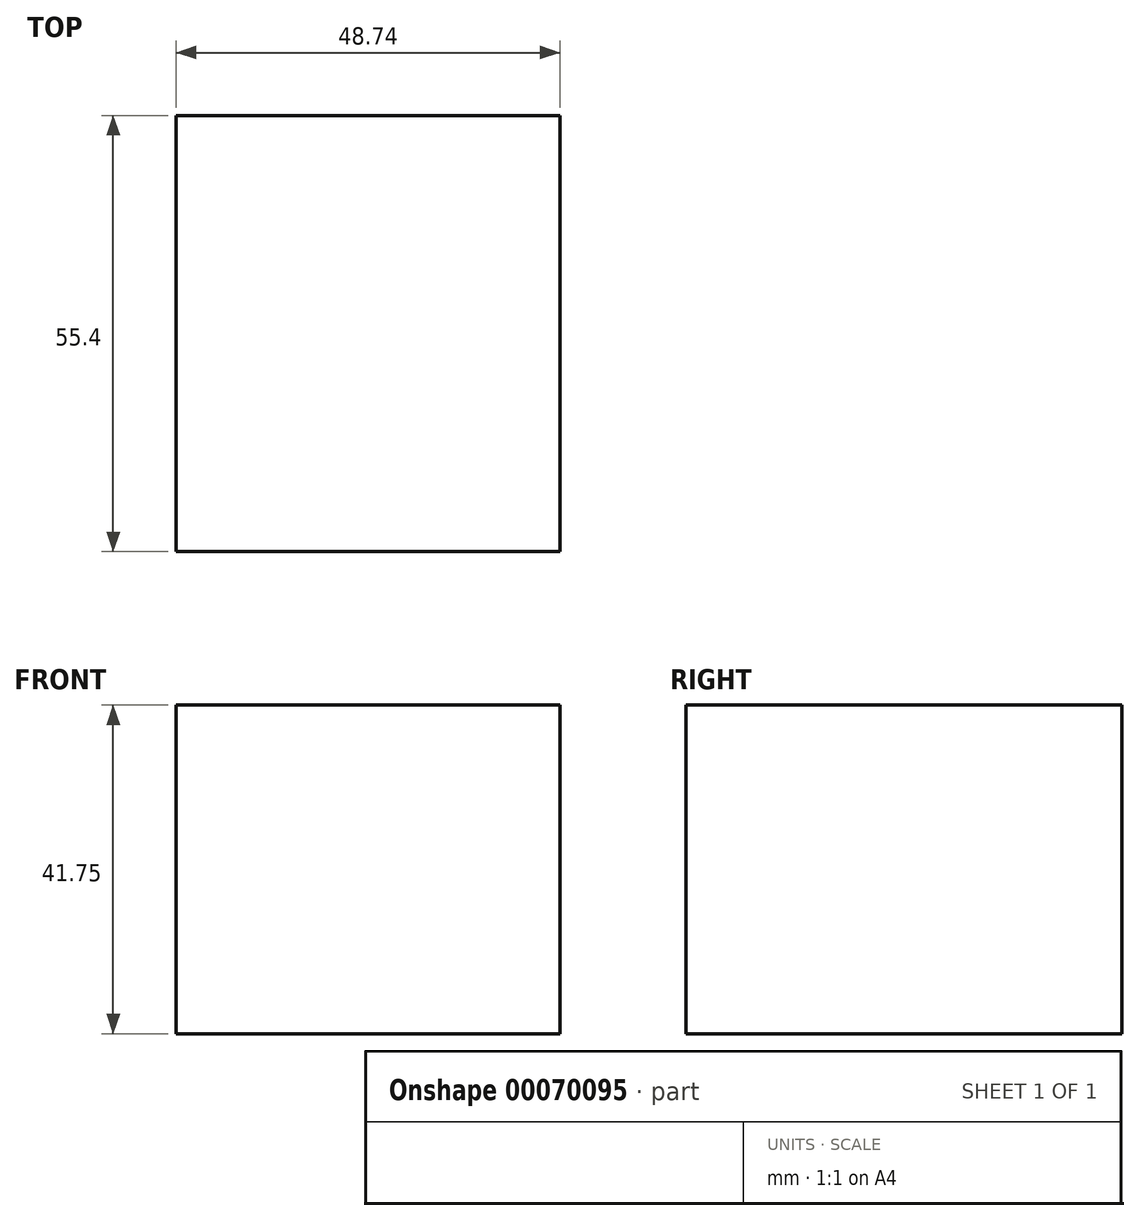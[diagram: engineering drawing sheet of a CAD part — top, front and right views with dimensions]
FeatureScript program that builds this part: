
annotation { "Feature Type Name" : "Feature", "Feature Type Description" : "" }
export const myFeature = defineFeature(function(context is Context, id is Id, definition is map)
    precondition{}
    {
        {
            var Q0;
            Q0=qCreatedBy(makeId("Front.planeOp"),FACE);
            var sketch = newSketch(context, id + "F0", { "sketchPlane" : qUnion([Q0])});
            skLineSegment(sketch, "E0.bottom", {"start": v(29.24, 17.57) * mm, "end": v(-19.5, 17.57) * mm});
            skLineSegment(sketch, "E0.top", {"start": v(29.24, -24.18) * mm, "end": v(-19.5, -24.18) * mm});
            skLineSegment(sketch, "E0.left", {"start": v(29.24, 17.57) * mm, "end": v(29.24, -24.18) * mm});
            skLineSegment(sketch, "E0.right", {"start": v(-19.5, 17.57) * mm, "end": v(-19.5, -24.18) * mm});
            skSolve(sketch);
        }
        {
            var Q0;
            Q0 = qSketchRegion(id + "F0", true);
            extrude(context, id + "F1", {"entities" : qUnion([Q0]), "depth" : 25.4 * mm});
        }
        {
            var Q0;
            Q0=makeQuery(id+"F1.opExtrude","CAP_FACE",FACE,{"disambiguationData":[OSD([sQuery(id+"F0.wireOp",EDGE,"E0.bottom"),sQuery(id+"F0.wireOp",EDGE,"E0.top"),sQuery(id+"F0.wireOp",EDGE,"E0.left"),sQuery(id+"F0.wireOp",EDGE,"E0.right")])],"isStart":false});
            extrude(context, id + "F2", {"entities" : qUnion([Q0]), "operationType" : NewBodyOperationType.ADD, "depth" : 30 * mm});
        }
    });
